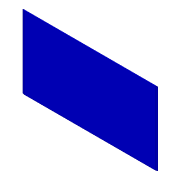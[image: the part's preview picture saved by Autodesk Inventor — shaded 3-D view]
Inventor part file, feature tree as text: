
AUTODESK INVENTOR PART (.ipt)
format: ipt  version: unknown  size: 526,848 bytes
history: native  units: in
note: dims shown in document units (in); Inventor stores cm internally (conversion verified against a paired STEP export)
features: chamfer x2, other x2, sketch x2, extrude x1
ambient origin geometry x8: Origin, YZ Plane, XZ Plane, XY Plane, X Axis, Y Axis, Z Axis, Center Point
bodies: Solid1 (feature_tree)
feature tree (7):
  extrude  "Extrusion1"  Depth=88.0in
  chamfer  "Chamfer1"  Distance=0.5in
  chamfer  "Chamfer3"  Distance=0.375in
  other  "Decal2"
  sketch  "Sketch1"  dims[d0=47.5in d1=88.0in d2=0.5in d3=0.0in d4=0.375in d5=0.125in d6=0.5085in]
  sketch  "Sketch3"  dims[d10=0.375in d11=0.125in d12=0.5085in]
  other  "Image2"
